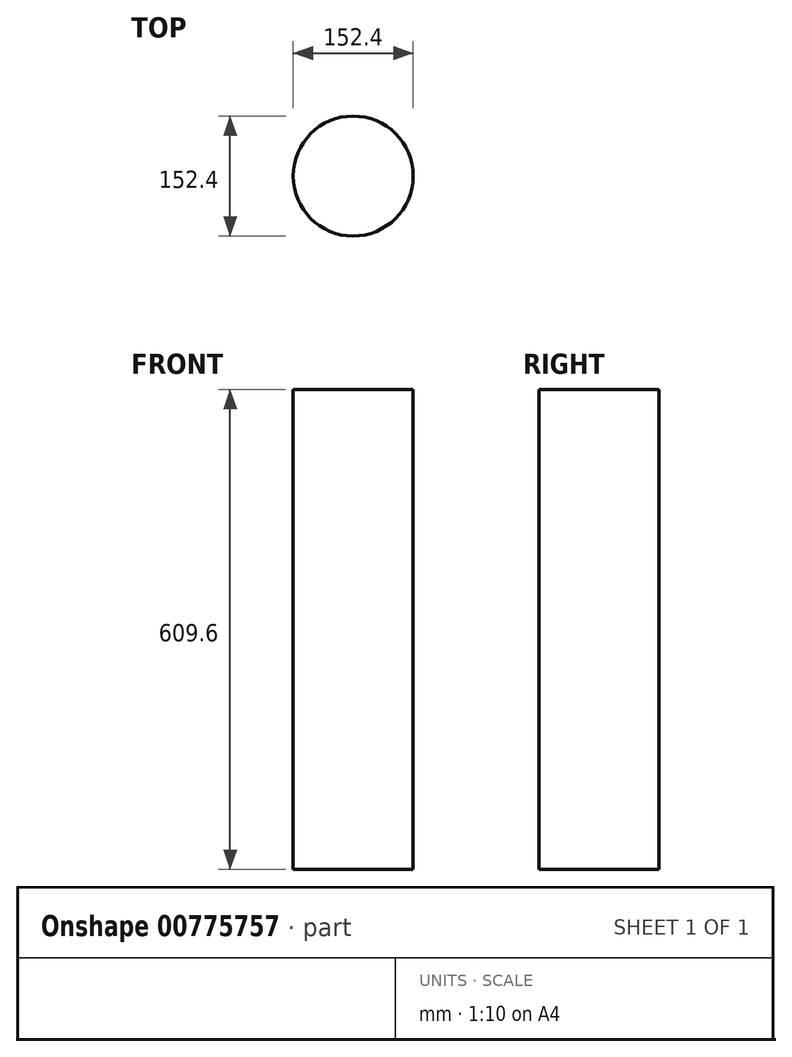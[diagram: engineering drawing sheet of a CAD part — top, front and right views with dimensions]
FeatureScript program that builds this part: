
annotation { "Feature Type Name" : "Feature", "Feature Type Description" : "" }
export const myFeature = defineFeature(function(context is Context, id is Id, definition is map)
    precondition{}
    {
        {
            var Q0;
            Q0=qCreatedBy(makeId("Top.planeOp"),FACE);
            var sketch = newSketch(context, id + "F0", { "sketchPlane" : qUnion([Q0])});
            skCircle(sketch, "E0", {"center": v(0, 0) * mm, "radius": 76.2 * mm});
            skSolve(sketch);
        }
        {
            var Q0;
            Q0 = qSketchRegion(id + "F0", true);
            extrude(context, id + "F1", {"entities" : qUnion([Q0]), "depth" : 609.6 * mm, "offsetDistance" : 25.4 * mm});
        }
    });
